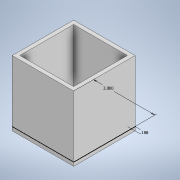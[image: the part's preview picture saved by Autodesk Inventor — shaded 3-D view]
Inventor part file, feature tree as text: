
AUTODESK INVENTOR PART (.ipt)
format: ipt  version: 2022 (Build 260153000, 153)  size: 99,840 bytes
history: native  units: in
note: dims shown in document units (in); Inventor stores cm internally (conversion verified against a paired STEP export)
features: extrude x2, sketch x1
ambient origin geometry x8: Origin, YZ Plane, XZ Plane, XY Plane, X Axis, Y Axis, Z Axis, Center Point
bodies: Solid1 (feature_tree)
feature tree (3):
  sketch  "Sketch1"  dims[d0=3.0in d1=0.1875in d2=0.1875in d3=0.0in d4=3.0in d5=0.0in]
  extrude  "Extrusion1"  Depth=0.1875in
  extrude  "Extrusion2"  Depth=0.1875in TaperAngle=0.0deg
